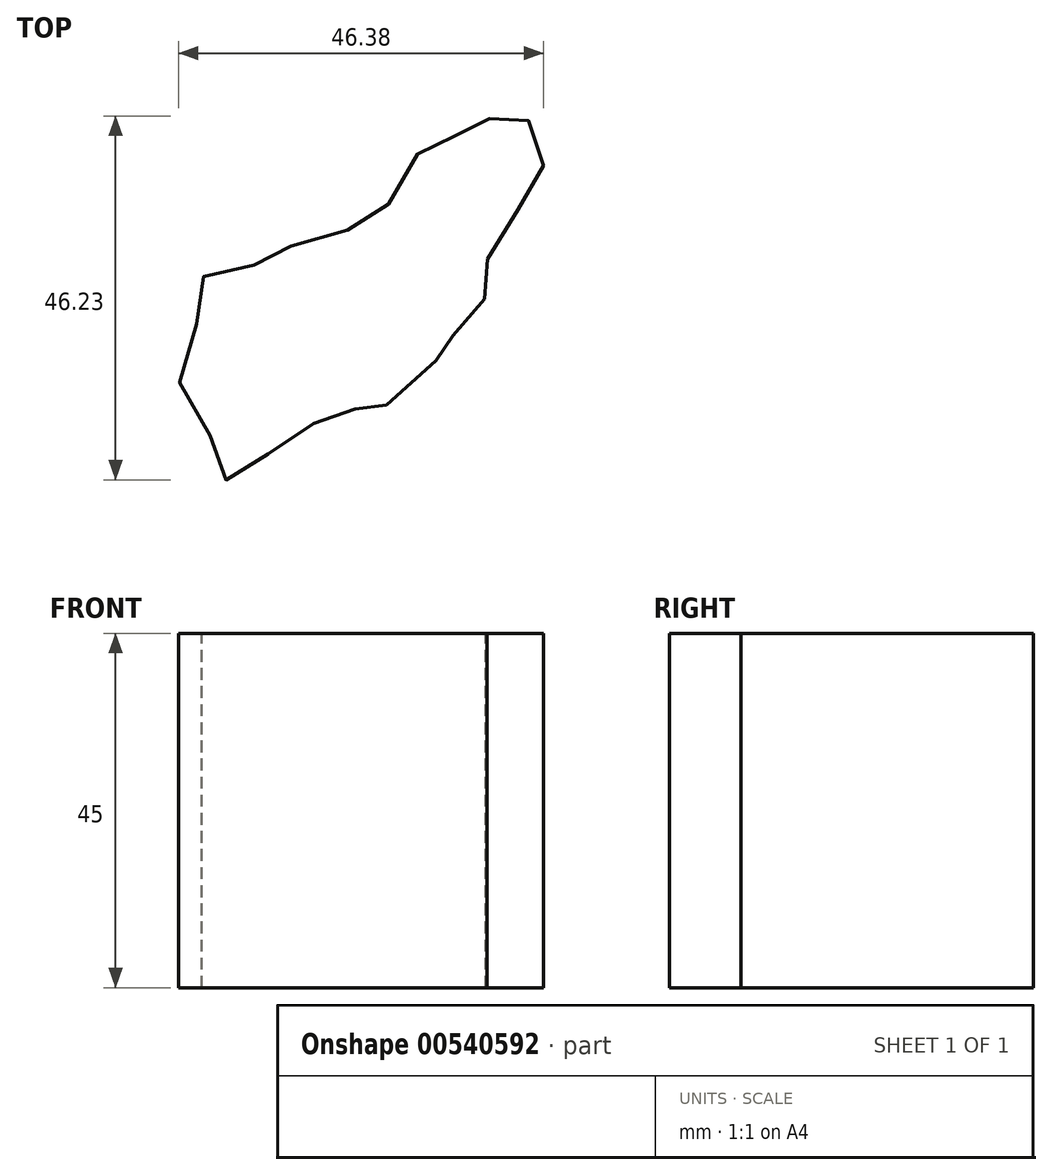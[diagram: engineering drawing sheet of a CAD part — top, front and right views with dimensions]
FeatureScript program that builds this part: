
annotation { "Feature Type Name" : "Feature", "Feature Type Description" : "" }
export const myFeature = defineFeature(function(context is Context, id is Id, definition is map)
    precondition{}
    {
        {
            var Q0;
            Q0=qCreatedBy(makeId("Top.planeOp"),FACE);
            var sketch = newSketch(context, id + "F0", { "sketchPlane" : qUnion([Q0])});
            skFitSpline(sketch, "E0", {"points": [v(-35.05, 1.87) * mm, v(-39.04, 9.42) * mm, v(-36.16, 18.07) * mm, v(-35.71, 22.28) * mm, v(-29.06, 23.61) * mm, v(-25.95, 25.39) * mm, v(-18.41, 27.83) * mm, v(-13.98, 29.6) * mm, v(-8.87, 37.14) * mm, v(-8.2, 38.47) * mm, v(-2, 40.7) * mm, v(0, 42.02) * mm, v(5.1, 42.25) * mm, v(5.54, 41.36) * mm, v(7.32, 35.37) * mm, v(3.55, 30.05) * mm, v(0, 23.4) * mm, v(0, 19.84) * mm, v(-3.1, 15.63) * mm, v(-5.55, 12.97) * mm, v(-6.21, 11.63) * mm, v(-13.3, 5.42) * mm, v(-15.08, 5.42) * mm, v(-18.41, 4.76) * mm, v(-23.07, 2.76) * mm, v(-29.28, -1.67) * mm, v(-33.27, -3.67) * mm, v(-35.05, 1.87) * mm]});
            skSolve(sketch);
        }
        {
            var Q0;
            Q0 = qSketchRegion(id + "F0", true);
            extrude(context, id + "F1", {"entities" : qUnion([Q0]), "depth" : 25 * mm, "offsetDistance" : 25 * mm});
        }
        {
            var Q0;
            Q0=makeQuery(id+"F1.opExtrude","CAP_FACE",FACE,{"disambiguationData":[OSD([sQuery(id+"F0.wireOp",EDGE,"E0")])],"isStart":false});
            extrude(context, id + "F2", {"entities" : qUnion([Q0]), "operationType" : NewBodyOperationType.ADD, "depth" : 20 * mm, "offsetDistance" : 25 * mm});
        }
    });
